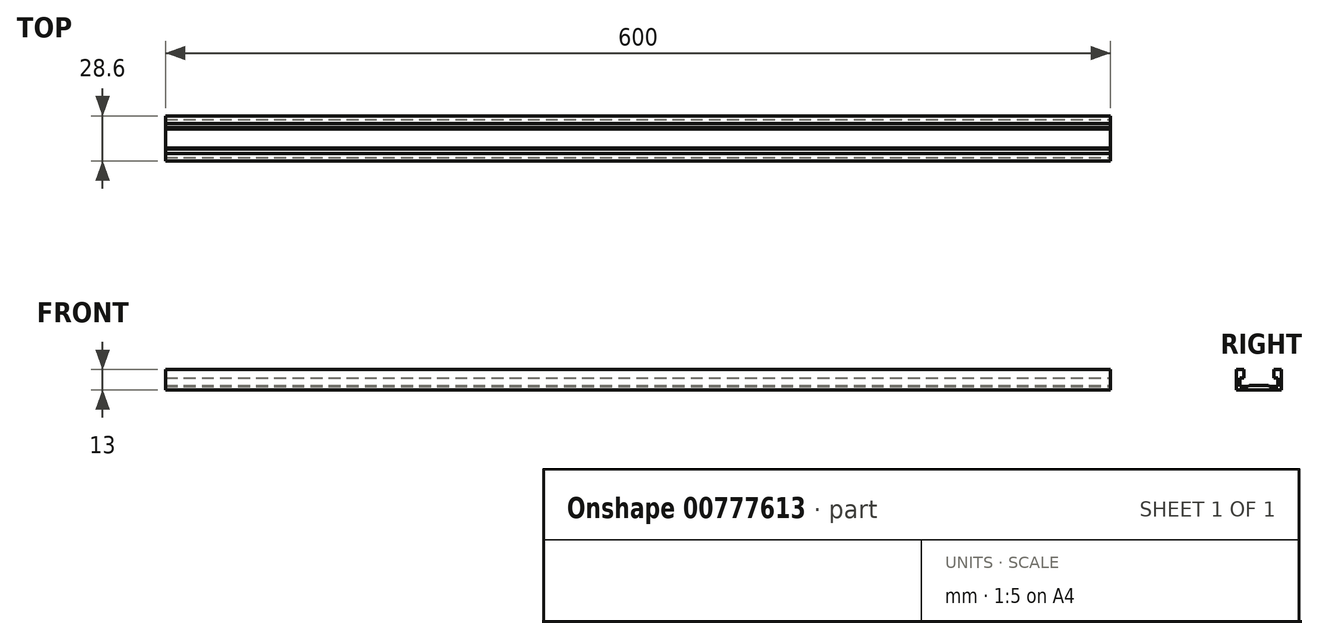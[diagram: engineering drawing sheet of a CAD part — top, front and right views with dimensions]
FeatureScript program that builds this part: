
annotation { "Feature Type Name" : "Feature", "Feature Type Description" : "" }
export const myFeature = defineFeature(function(context is Context, id is Id, definition is map)
    precondition{}
    {
        {
            var Q0;
            Q0=qCreatedBy(makeId("Right.planeOp"),FACE);
            var sketch = newSketch(context, id + "F0", { "sketchPlane" : qUnion([Q0])});
            skLineSegment(sketch, "E0", {"start": v(0, 0) * mm, "end": v(14.3, 0) * mm});
            skLineSegment(sketch, "E1", {"start": v(14.3, 0) * mm, "end": v(14.3, 13) * mm});
            skLineSegment(sketch, "E2", {"start": v(14.3, 13) * mm, "end": v(9.6, 13) * mm});
            skLineSegment(sketch, "E3", {"start": v(9.6, 13) * mm, "end": v(9.6, 7.8) * mm});
            skLineSegment(sketch, "E4", {"start": v(9.6, 7.8) * mm, "end": v(12.1, 7.8) * mm});
            skLineSegment(sketch, "E5", {"start": v(12.1, 7.8) * mm, "end": v(12.1, 2.2) * mm});
            skLineSegment(sketch, "E6", {"start": v(12.1, 2.2) * mm, "end": v(6.8, 2.2) * mm});
            skLineSegment(sketch, "E7", {"start": v(6.8, 2.2) * mm, "end": v(6, 3) * mm});
            skLineSegment(sketch, "E8", {"start": v(6, 3) * mm, "end": v(0, 3) * mm});
            skLineSegment(sketch, "E9.MirrorCS", {"start": v(-6.8, 2.2) * mm, "end": v(-6, 3) * mm});
            skLineSegment(sketch, "E10.MirrorCS", {"start": v(-9.6, 13) * mm, "end": v(-9.6, 7.8) * mm});
            skLineSegment(sketch, "E11.MirrorCS", {"start": v(-9.6, 7.8) * mm, "end": v(-12.1, 7.8) * mm});
            skLineSegment(sketch, "E12.MirrorCS", {"start": v(0, 0) * mm, "end": v(-14.3, 0) * mm});
            skLineSegment(sketch, "E13.MirrorCS", {"start": v(-14.3, 13) * mm, "end": v(-9.6, 13) * mm});
            skLineSegment(sketch, "E14.MirrorCS", {"start": v(-12.1, 7.8) * mm, "end": v(-12.1, 2.2) * mm});
            skLineSegment(sketch, "E15.MirrorCS", {"start": v(-14.3, 0) * mm, "end": v(-14.3, 13) * mm});
            skLineSegment(sketch, "E16.MirrorCS", {"start": v(-6, 3) * mm, "end": v(0, 3) * mm});
            skLineSegment(sketch, "E17.MirrorCS", {"start": v(-12.1, 2.2) * mm, "end": v(-6.8, 2.2) * mm});
            skSolve(sketch);
        }
        {
            var Q0;
            Q0 = qSketchRegion(id + "F0", true);
            extrude(context, id + "F1", {"entities" : qUnion([Q0]), "oppositeDirection" : true, "depth" : 600 * mm, "offsetDistance" : 25 * mm});
        }
    });
